# Revit family: Schlüter-BEKOTEC-THERM-HV-AS 5-fach Heizkreisvert- Anschluss-Set 16 mm
name_source: partatom
category: Sanitärinstallationen
revit_build: Autodesk Revit 2018 (Build: 20170223_1515(x64)
units: mm (PartAtom-declared; Revit-internal decimal feet)

## family parameters
Arbeitsebenenbasiert = Nein
Beim Laden mit Abzugskörper schneiden = Nein
Bemaßung runder Anschluss = Durchmesser verwenden
Gemeinsam genutzt = Nein
Immer vertikal = Ja
OmniClass-Nummer = 23.45.00.00
OmniClass-Titel = Sanitary, Laundry, and Cleaning Equipment
Raumberechnungspunkt = Nein
Teiletyp = Normal

## types (1)
- Schlüter-BEKOTEC-THERM-HV-AS 5-fach Heizkreisvert- Anschluss-Set 16 mm
    Abwasserrohrverbindung = Nein
    Anzahl Heizkreise = 5
    BIM = https://media.live.bim.site
    BIMSITE_PRODUCT_ID = b0a34683e1d321df5505625190c2895a3c4e01cc
    Beschreibung = Schlüter®-BEKOTEC-THERM ist die sichere Belagskonstruktionstechnik mit geringer Aufbauhöhe. In Verbindung mit der zugehörigen Heiz- und Regeltechnik ergibt sich ein energiesparendes und schnell reagierendes Fußbodenheizsystem mit besonders niedriger Vorlauftemperatur.
    CWFU = 0
    Datenblatt = https://media.live.bim.site
    Datenblatt 1 = https://media.live.bim.site
    Datenblatt 2 = https://media.live.bim.site
    Durchmesser [mm] = 16
    GTIN = 4011832059193
    HAN = BTHV5AS
    HW-Verbindung = Nein
    HWFU = 0
    HZPID = 7322457
    HZPSID = 10000136
    Handbuch = https://media.live.bim.site
    HeinzeBIM = https://www.heinze.de
    Hersteller = Schlüter-Systems
    Ist System = Nein
    Ist Zubehör = Nein
    KW-Verbindung = Nein
    Kosten = 0 $
    Länge [mm] Number = 347000
    Lüftungsverbindung = Nein
    Nennweite DN = 25
    Produktseite = https://media.live.bim.site
    Typname = Schlüter-BEKOTEC-THERM-HV/AS 5-fach Heizkreisvert. Anschluss-Set 16 mm
    URL = https://www.schlueter.de
    WFU = 0

## geometry (parser evidence)
native form markers: Sweep x13
no freeform markers — native parametric forms only
